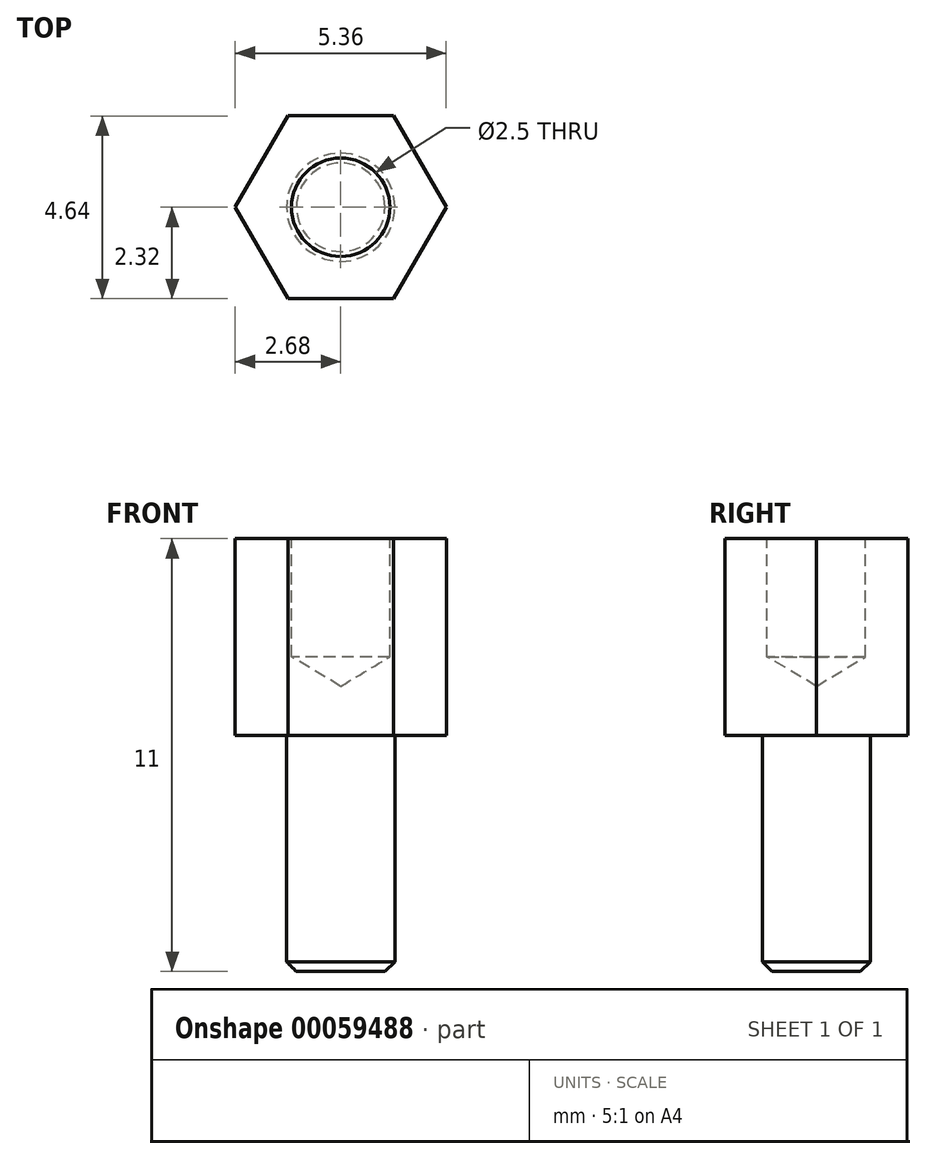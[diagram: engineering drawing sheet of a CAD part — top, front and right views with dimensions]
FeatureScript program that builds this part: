
annotation { "Feature Type Name" : "Feature", "Feature Type Description" : "" }
export const myFeature = defineFeature(function(context is Context, id is Id, definition is map)
    precondition{}
    {
        {
            var Q0;
            Q0=qCreatedBy(makeId("Top.planeOp"),FACE);
            var sketch = newSketch(context, id + "F0", { "sketchPlane" : qUnion([Q0])});
            skCircle(sketch, "E0.cCircle", {"center": v(0, 0) * mm, "radius": 2.33 * mm, "construction": true});
            skLineSegment(sketch, "E0.0", {"start": v(-1.34, 2.33) * mm, "end": v(1.34, 2.33) * mm});
            skLineSegment(sketch, "E0.1", {"start": v(1.34, 2.33) * mm, "end": v(2.68, 0) * mm});
            skLineSegment(sketch, "E0.2", {"start": v(2.68, 0) * mm, "end": v(1.34, -2.32) * mm});
            skLineSegment(sketch, "E0.3", {"start": v(1.34, -2.32) * mm, "end": v(-1.34, -2.33) * mm});
            skLineSegment(sketch, "E0.4", {"start": v(-1.34, -2.32) * mm, "end": v(-2.68, 0) * mm});
            skLineSegment(sketch, "E0.5", {"start": v(-2.68, 0) * mm, "end": v(-1.34, 2.32) * mm});
            skPoint(sketch, "E0.0.midPoint", {"position": v(0, 2.33) * mm});
            skSolve(sketch);
        }
        {
            var Q0;
            Q0=makeQuery(id+"F0.imprint","IMPRINT",FACE,{"disambiguationData":[TD([[makeQuery(id+"F0.imprint","IMPRINT",EDGE,{"derivedFrom":sQuery(id+"F0.wireOp",EDGE,"E0.0")}),-1.0]])]});
            extrude(context, id + "F1", {"entities" : qUnion([Q0]), "depth" : 5 * mm});
        }
        {
            var Q0;
            Q0=makeQuery(id+"F1.opExtrude","CAP_FACE",FACE,{"disambiguationData":[OSD([sQuery(id+"F0.wireOp",EDGE,"E0.0"),sQuery(id+"F0.wireOp",EDGE,"E0.1"),sQuery(id+"F0.wireOp",EDGE,"E0.2"),sQuery(id+"F0.wireOp",EDGE,"E0.3"),sQuery(id+"F0.wireOp",EDGE,"E0.4"),sQuery(id+"F0.wireOp",EDGE,"E0.5")])],"isStart":false});
            var sketch = newSketch(context, id + "F2", { "sketchPlane" : qUnion([Q0])});
            skPoint(sketch, "E1.0", {"position": v(0, 0) * mm});
            skSolve(sketch);
        }
        {
            var Q0;
            Q0=sQuery(id+"F2.wireOp",VERTEX,"E1.0");
            var Q1;
            Q1=makeQuery(id+"F1.opExtrude","SWEPT_BODY",BODY,{"disambiguationData":[OSD([sQuery(id+"F0.wireOp",EDGE,"E0.0"),sQuery(id+"F0.wireOp",EDGE,"E0.1"),sQuery(id+"F0.wireOp",EDGE,"E0.2"),sQuery(id+"F0.wireOp",EDGE,"E0.3"),sQuery(id+"F0.wireOp",EDGE,"E0.4"),sQuery(id+"F0.wireOp",EDGE,"E0.5")])]});
            hole(context, id + "F3", {"style" : HoleStyle.SIMPLE, "holeDiameter" : 2.5 * mm, "endStyle" : HoleEndStyle.BLIND, "holeDepth" : 3 * mm, "locations" : qUnion([Q0]), "scope" : qUnion([Q1])});
        }
        {
            var Q0;
            Q0=makeQuery(id+"F1.opExtrude","CAP_FACE",FACE,{"disambiguationData":[OSD([sQuery(id+"F0.wireOp",EDGE,"E0.0"),sQuery(id+"F0.wireOp",EDGE,"E0.1"),sQuery(id+"F0.wireOp",EDGE,"E0.2"),sQuery(id+"F0.wireOp",EDGE,"E0.3"),sQuery(id+"F0.wireOp",EDGE,"E0.4"),sQuery(id+"F0.wireOp",EDGE,"E0.5")])],"isStart":true});
            var sketch = newSketch(context, id + "F4", { "sketchPlane" : qUnion([Q0])});
            skCircle(sketch, "E2", {"center": v(0, 0) * mm, "radius": 1.38 * mm});
            skSolve(sketch);
        }
        {
            var Q0;
            Q0=makeQuery(id+"F4.imprint","IMPRINT",FACE,{"disambiguationData":[TD([[makeQuery(id+"F4.imprint","IMPRINT",EDGE,{"derivedFrom":sQuery(id+"F4.wireOp",EDGE,"E2")}),1.0]])]});
            extrude(context, id + "F5", {"entities" : qUnion([Q0]), "operationType" : NewBodyOperationType.ADD, "depth" : 6 * mm});
        }
        {
            var Q0;
            Q0=makeQuery(id+"F5.opExtrude","CAP_EDGE",EDGE,{"disambiguationData":[OSD([sQuery(id+"F4.wireOp",EDGE,"E2")])],"isStart":false});
            chamfer(context, id + "F6", {"entities" : qUnion([Q0]), "width" : .25 * mm, "tangentPropagation" : true});
        }
    });
